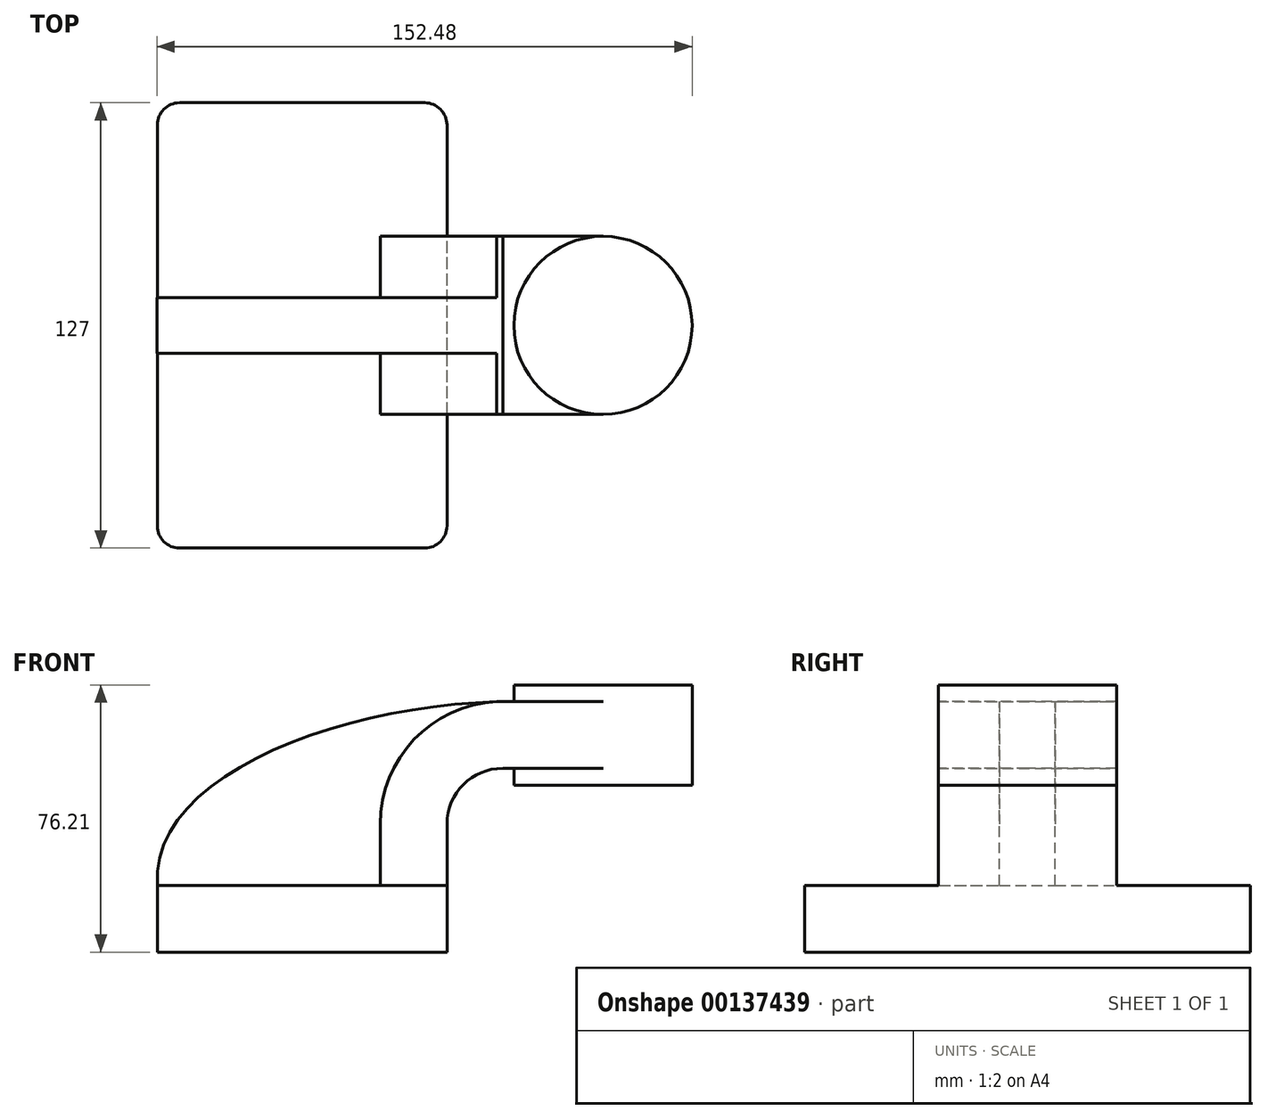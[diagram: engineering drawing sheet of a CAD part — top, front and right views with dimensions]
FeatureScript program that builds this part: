
annotation { "Feature Type Name" : "Feature", "Feature Type Description" : "" }
export const myFeature = defineFeature(function(context is Context, id is Id, definition is map)
    precondition{}
    {
        {
            var Q0;
            Q0=qCreatedBy(makeId("Front.planeOp"),FACE);
            var sketch = newSketch(context, id + "F0", { "sketchPlane" : qUnion([Q0])});
            skLineSegment(sketch, "E0.bottom", {"start": v(-41.27, -9.52) * mm, "end": v(41.28, -9.52) * mm});
            skLineSegment(sketch, "E0.top", {"start": v(-41.28, 9.52) * mm, "end": v(41.27, 9.52) * mm});
            skLineSegment(sketch, "E0.left", {"start": v(-41.27, -9.52) * mm, "end": v(-41.28, 9.52) * mm});
            skLineSegment(sketch, "E0.right", {"start": v(41.28, -9.52) * mm, "end": v(41.27, 9.52) * mm});
            skPoint(sketch, "E0.middle", {"position": v(0, 0) * mm});
            skLineSegment(sketch, "E1.bottom", {"start": v(60.32, 38.1) * mm, "end": v(111.13, 38.1) * mm});
            skLineSegment(sketch, "E1.top", {"start": v(60.32, 66.68) * mm, "end": v(111.13, 66.68) * mm});
            skLineSegment(sketch, "E1.left", {"start": v(60.32, 38.1) * mm, "end": v(60.32, 66.67) * mm});
            skLineSegment(sketch, "E1.right", {"start": v(111.13, 38.1) * mm, "end": v(111.13, 66.67) * mm});
            skPoint(sketch, "E1.middle", {"position": v(85.73, 52.39) * mm});
            skLineSegment(sketch, "E2", {"start": v(41.27, 9.52) * mm, "end": v(41.27, 27) * mm});
            skArc(sketch, "E3", {"start": v(41.27, 27) * mm, "mid": v(45.92, 38.23) * mm, "end": v(57.15, 42.88) * mm});
            skLineSegment(sketch, "E4", {"start": v(57.15, 42.88) * mm, "end": v(85.73, 42.88) * mm});
            skLineSegment(sketch, "E5", {"start": v(85.73, 38.1) * mm, "end": v(85.73, 66.68) * mm});
            skLineSegment(sketch, "E6.0", {"start": v(57.15, 61.93) * mm, "end": v(85.73, 61.93) * mm});
            skArc(sketch, "E6.1", {"start": v(22.23, 27) * mm, "mid": v(32.45, 51.7) * mm, "end": v(57.15, 61.93) * mm});
            skLineSegment(sketch, "E6.2", {"start": v(22.22, 9.52) * mm, "end": v(22.22, 27) * mm});
            skFitSpline(sketch, "E7", {"points": [v(-41.27, 9.53) * mm, v(57.15, 61.93) * mm], "startDerivative": vector(-6.93, 94.8) * mm, "endDerivative": vector(136.8, 2.66) * mm});
            skSolve(sketch);
        }
        {
            var Q0;
            Q0=makeQuery(id+"F0.imprint","IMPRINT",FACE,{"disambiguationData":[TD([[makeQuery(id+"F0.imprint","IMPRINT",EDGE,{"derivedFrom":sQuery(id+"F0.wireOp",EDGE,"E0.bottom")}),1.0]])]});
            extrude(context, id + "F1", {"entities" : qUnion([Q0]), "endBound" : BoundingType.SYMMETRIC, "depth" : 127 * mm});
        }
        {
            var Q0;
            {var subQ1=sQuery(id+"F0.wireOp",EDGE,"E2");Q0=makeQuery(id+"F0.imprint","IMPRINT",FACE,{"disambiguationData":[TD([[makeQuery(id+"F0.imprint","IMPRINT",EDGE,{"derivedFrom":subQ1}),1.0]])]});}
            var Q1;
            {var subQ0=sQuery(id+"F0.wireOp",EDGE,"E4");var subQ1=sQuery(id+"F0.wireOp",EDGE,"E1.left");var subQ2=makeQuery(id+"F0.imprint","INTERSECT",VERTEX,{"derivedFrom":[subQ1,subQ0]});Q1=makeQuery(id+"F0.imprint","IMPRINT",FACE,{"disambiguationData":[TD([[makeQuery(id+"F0.imprint","IMPRINT",EDGE,{"disambiguationData":[TD([[subQ2,-1.0]])],"derivedFrom":subQ1}),-1.0]])]});}
            extrude(context, id + "F2", {"entities" : qUnion([Q0, Q1]), "operationType" : NewBodyOperationType.ADD, "endBound" : BoundingType.SYMMETRIC, "depth" : 50.8 * mm});
        }
        {
            var Q0;
            {var subQ3=sQuery(id+"F0.wireOp",EDGE,"E6.2");Q0=makeQuery(id+"F0.imprint","IMPRINT",FACE,{"disambiguationData":[TD([[makeQuery(id+"F0.imprint","IMPRINT",EDGE,{"derivedFrom":subQ3}),1.0]])]});}
            extrude(context, id + "F3", {"entities" : qUnion([Q0]), "operationType" : NewBodyOperationType.ADD, "endBound" : BoundingType.SYMMETRIC, "depth" : 15.88 * mm});
        }
        {
            var Q0;
            {var subQ4=sQuery(id+"F0.wireOp",EDGE,"E1.right");Q0=makeQuery(id+"F0.imprint","IMPRINT",FACE,{"disambiguationData":[TD([[makeQuery(id+"F0.imprint","IMPRINT",EDGE,{"derivedFrom":subQ4}),1.0]])]});}
            var Q1;
            Q1=sQuery(id+"F0.wireOp",EDGE,"E5");
            revolve(context, id + "F4", {"operationType" : NewBodyOperationType.ADD, "entities" : qUnion([Q0]), "axis" : qUnion([Q1]), "revolveType" : RevolveType.FULL});
        }
        {
            var Q0;
            Q0=makeQuery(id+"F1.opExtrude","CAP_EDGE",EDGE,{"disambiguationData":[OSD([sQuery(id+"F0.wireOp",EDGE,"E0.right")])],"isStart":false});
            var Q1;
            Q1=makeQuery(id+"F1.opExtrude","CAP_EDGE",EDGE,{"disambiguationData":[OSD([sQuery(id+"F0.wireOp",EDGE,"E0.left")])],"isStart":false});
            var Q2;
            Q2=makeQuery(id+"F1.opExtrude","CAP_EDGE",EDGE,{"disambiguationData":[OSD([sQuery(id+"F0.wireOp",EDGE,"E0.left")])],"isStart":true});
            var Q3;
            Q3=makeQuery(id+"F1.opExtrude","CAP_EDGE",EDGE,{"disambiguationData":[OSD([sQuery(id+"F0.wireOp",EDGE,"E0.right")])],"isStart":true});
            fillet(context, id + "F5", {"entities" : qUnion([Q0, Q1, Q2, Q3]), "radius" : 6.35 * mm, "tangentPropagation" : true, "allowEdgeOverflow" : false});
        }
    });
